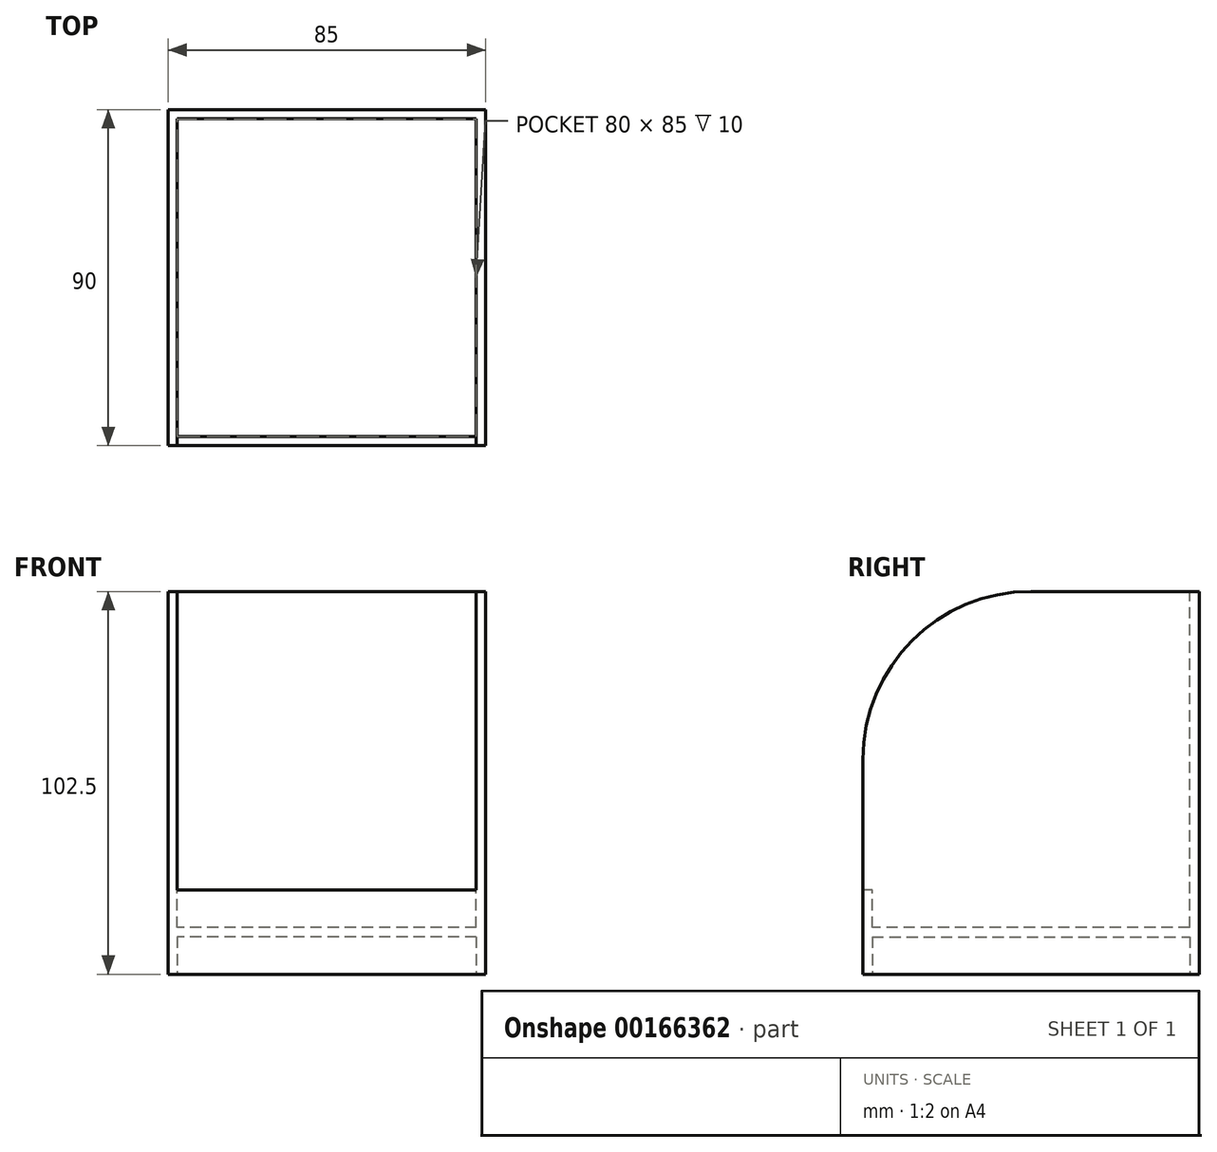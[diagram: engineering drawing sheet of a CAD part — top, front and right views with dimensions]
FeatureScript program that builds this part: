
annotation { "Feature Type Name" : "Feature", "Feature Type Description" : "" }
export const myFeature = defineFeature(function(context is Context, id is Id, definition is map)
    precondition{}
    {
        {
            var Q0;
            Q0=qCreatedBy(makeId("Top.planeOp"),FACE);
            var sketch = newSketch(context, id + "F0", { "sketchPlane" : qUnion([Q0])});
            skLineSegment(sketch, "E0.bottom", {"start": v(-54.44, -48.48) * mm, "end": v(30.56, -48.48) * mm});
            skLineSegment(sketch, "E0.top", {"start": v(-54.44, 41.52) * mm, "end": v(30.56, 41.52) * mm});
            skLineSegment(sketch, "E0.left", {"start": v(-54.44, -48.48) * mm, "end": v(-54.44, 41.52) * mm});
            skLineSegment(sketch, "E0.right", {"start": v(30.56, -48.48) * mm, "end": v(30.56, 41.52) * mm});
            skSolve(sketch);
        }
        {
            var Q0;
            Q0=makeQuery(id+"F0.imprint","IMPRINT",FACE,{"disambiguationData":[TD([[makeQuery(id+"F0.imprint","IMPRINT",EDGE,{"derivedFrom":sQuery(id+"F0.wireOp",EDGE,"E0.bottom")}),1.0]])]});
            extrude(context, id + "F1", {"entities" : qUnion([Q0]), "depth" : 102.5 * mm});
        }
        {
            var Q0;
            Q0=makeQuery(id+"F1.opExtrude","CAP_FACE",FACE,{"disambiguationData":[OSD([sQuery(id+"F0.wireOp",EDGE,"E0.bottom"),sQuery(id+"F0.wireOp",EDGE,"E0.top"),sQuery(id+"F0.wireOp",EDGE,"E0.left"),sQuery(id+"F0.wireOp",EDGE,"E0.right")])],"isStart":true});
            var sketch = newSketch(context, id + "F2", { "sketchPlane" : qUnion([Q0])});
            skLineSegment(sketch, "E1.0", {"start": v(-51.94, 45.98) * mm, "end": v(-51.94, -39.02) * mm});
            skLineSegment(sketch, "E1.1", {"start": v(28.06, 45.98) * mm, "end": v(-51.94, 45.98) * mm});
            skLineSegment(sketch, "E1.2", {"start": v(28.06, -39.02) * mm, "end": v(28.06, 45.98) * mm});
            skLineSegment(sketch, "E1.3", {"start": v(-51.94, -39.02) * mm, "end": v(28.06, -39.02) * mm});
            skSolve(sketch);
        }
        {
            var Q0;
            Q0=makeQuery(id+"F2.imprint","IMPRINT",FACE,{"disambiguationData":[TD([[makeQuery(id+"F2.imprint","IMPRINT",EDGE,{"derivedFrom":sQuery(id+"F2.wireOp",EDGE,"E1.0")}),1.0]])]});
            var Q1;
            Q1=sQuery(id+"F2.wireOp",EDGE,"E1.0");
            var Q2;
            Q2=sQuery(id+"F2.wireOp",EDGE,"E1.1");
            var Q3;
            Q3=sQuery(id+"F2.wireOp",EDGE,"E1.2");
            var Q4;
            Q4=sQuery(id+"F2.wireOp",EDGE,"E1.3");
            extrude(context, id + "F3", {"entities" : qUnion([Q0]), "operationType" : NewBodyOperationType.REMOVE, "surfaceEntities" : qUnion([Q1, Q2, Q3, Q4]), "oppositeDirection" : true, "depth" : 10 * mm});
        }
        {
            var Q0;
            Q0=makeQuery(id+"F1.opExtrude","CAP_FACE",FACE,{"disambiguationData":[OSD([sQuery(id+"F0.wireOp",EDGE,"E0.bottom"),sQuery(id+"F0.wireOp",EDGE,"E0.top"),sQuery(id+"F0.wireOp",EDGE,"E0.left"),sQuery(id+"F0.wireOp",EDGE,"E0.right")])],"isStart":false});
            var sketch = newSketch(context, id + "F4", { "sketchPlane" : qUnion([Q0])});
            skLineSegment(sketch, "E2.0", {"start": v(-51.94, 39.02) * mm, "end": v(-51.94, -45.98) * mm});
            skLineSegment(sketch, "E2.1", {"start": v(28.06, 39.02) * mm, "end": v(-51.94, 39.02) * mm});
            skLineSegment(sketch, "E2.2", {"start": v(28.06, -45.98) * mm, "end": v(28.06, 39.02) * mm});
            skLineSegment(sketch, "E2.3", {"start": v(-51.94, -45.98) * mm, "end": v(28.06, -45.98) * mm});
            skSolve(sketch);
        }
        {
            var Q0;
            Q0=makeQuery(id+"F4.imprint","IMPRINT",FACE,{"disambiguationData":[TD([[makeQuery(id+"F4.imprint","IMPRINT",EDGE,{"derivedFrom":sQuery(id+"F4.wireOp",EDGE,"E2.0")}),1.0]])]});
            extrude(context, id + "F5", {"entities" : qUnion([Q0]), "operationType" : NewBodyOperationType.REMOVE, "oppositeDirection" : true, "depth" : 90 * mm});
        }
        {
            var Q0;
            Q0=makeQuery(id+"F1.opExtrude","SWEPT_FACE",FACE,{"disambiguationData":[OSD([sQuery(id+"F0.wireOp",EDGE,"E0.bottom")])]});
            var sketch = newSketch(context, id + "F6", { "sketchPlane" : qUnion([Q0])});
            skLineSegment(sketch, "E3.bottom", {"start": v(-51.94, 102.5) * mm, "end": v(28.06, 102.5) * mm});
            skLineSegment(sketch, "E3.top", {"start": v(-51.94, 22.5) * mm, "end": v(28.06, 22.5) * mm});
            skLineSegment(sketch, "E3.left", {"start": v(-51.94, 102.5) * mm, "end": v(-51.94, 22.5) * mm});
            skLineSegment(sketch, "E3.right", {"start": v(28.06, 102.5) * mm, "end": v(28.06, 22.5) * mm});
            skSolve(sketch);
        }
        {
            var Q0;
            Q0 = qSketchRegion(id + "F6", true);
            extrude(context, id + "F7", {"entities" : qUnion([Q0]), "operationType" : NewBodyOperationType.REMOVE, "oppositeDirection" : true, "depth" : 25 * mm});
        }
        {
            var Q0;
            {var subQ0=sQuery(id+"F0.wireOp",EDGE,"E0.left");var subQ1=sQuery(id+"F0.wireOp",EDGE,"E0.bottom");Q0=makeQuery(id+"F7.boolean.opBoolean","SPLIT",EDGE,{"disambiguationData":[TD([makeQuery(id+"F1.opExtrude","SWEPT_FACE",FACE,{"disambiguationData":[OSD([subQ0])]})])],"derivedFrom":makeQuery(id+"F1.opExtrude","CAP_EDGE",EDGE,{"disambiguationData":[OSD([subQ1])],"isStart":false})});}
            var Q1;
            {var subQ0=sQuery(id+"F0.wireOp",EDGE,"E0.right");var subQ1=sQuery(id+"F0.wireOp",EDGE,"E0.bottom");Q1=makeQuery(id+"F7.boolean.opBoolean","SPLIT",EDGE,{"disambiguationData":[TD([makeQuery(id+"F1.opExtrude","SWEPT_FACE",FACE,{"disambiguationData":[OSD([subQ0])]})])],"derivedFrom":makeQuery(id+"F1.opExtrude","CAP_EDGE",EDGE,{"disambiguationData":[OSD([subQ1])],"isStart":false})});}
            fillet(context, id + "F8", {"entities" : qUnion([Q0, Q1]), "radius" : 45 * mm, "tangentPropagation" : true, "allowEdgeOverflow" : false});
        }
    });
